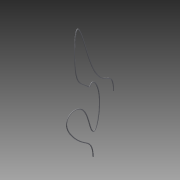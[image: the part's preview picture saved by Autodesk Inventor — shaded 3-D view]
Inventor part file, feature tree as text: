
AUTODESK INVENTOR PART (.ipt)
format: ipt  version: 2015 (Build 190159000, 159)  size: 196,608 bytes
history: native  units: in
note: dims shown in document units (in); Inventor stores cm internally (conversion verified against a paired STEP export)
features: sketch x3, plane x1, sweep x1
ambient origin geometry x8: Origin, YZ Plane, XZ Plane, XY Plane, X Axis, Y Axis, Z Axis, Center Point
bodies: Body1 (feature_tree)
feature tree (5):
  sketch  "Sketch1"  dims[d1=0.0in d2=0.0in]
  sketch  "Sketch2"
  plane  "Work Plane1"
  sweep  "Sweep2"
  sketch  "Sketch3"
